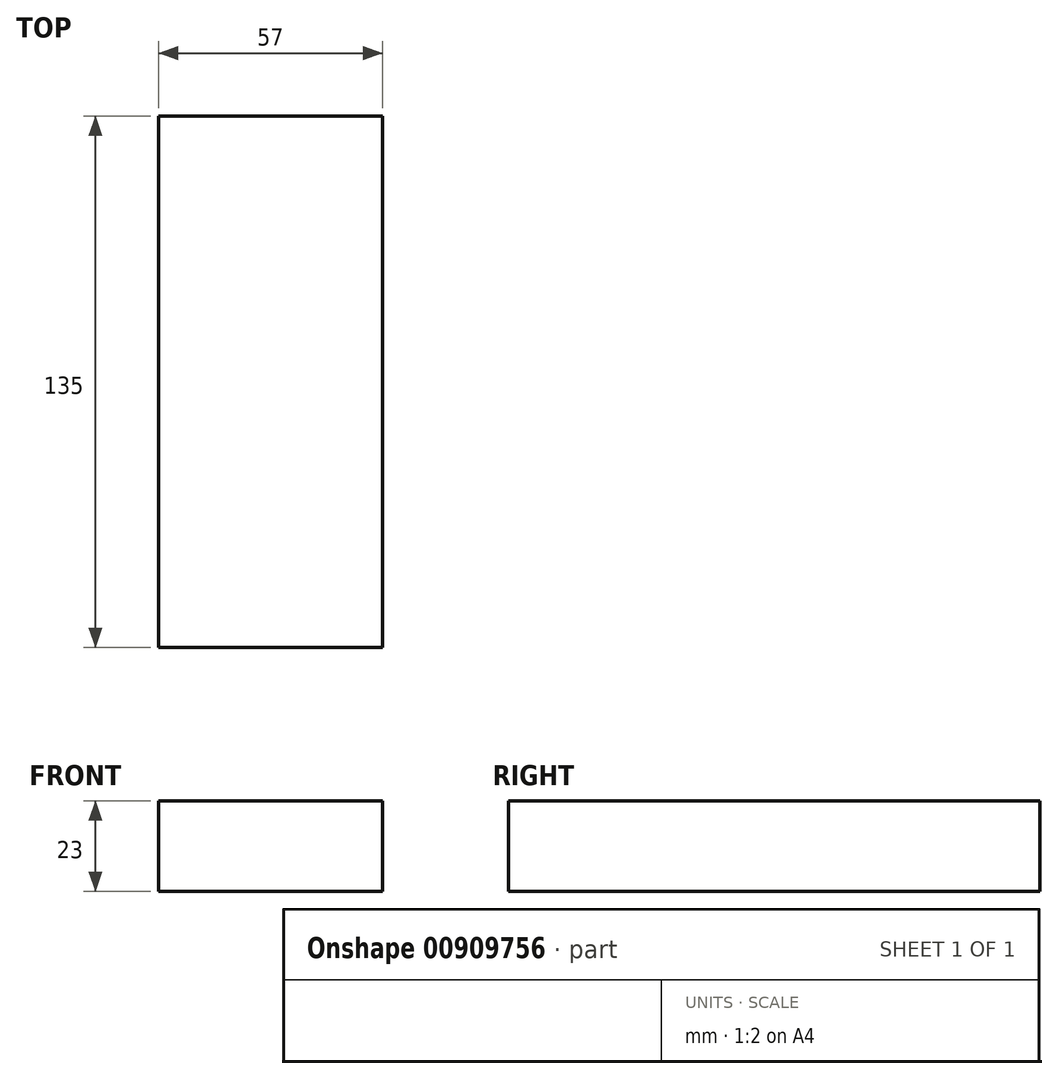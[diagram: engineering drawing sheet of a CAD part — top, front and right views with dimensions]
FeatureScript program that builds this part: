
annotation { "Feature Type Name" : "Feature", "Feature Type Description" : "" }
export const myFeature = defineFeature(function(context is Context, id is Id, definition is map)
    precondition{}
    {
        {
            var Q0;
            Q0=qCreatedBy(makeId("Top.planeOp"),FACE);
            var sketch = newSketch(context, id + "F0", { "sketchPlane" : qUnion([Q0])});
            skLineSegment(sketch, "E0.bottom", {"start": v(28.5, 67.5) * mm, "end": v(-28.5, 67.5) * mm});
            skLineSegment(sketch, "E0.top", {"start": v(28.5, -67.5) * mm, "end": v(-28.5, -67.5) * mm});
            skLineSegment(sketch, "E0.left", {"start": v(28.5, 67.5) * mm, "end": v(28.5, -67.5) * mm});
            skLineSegment(sketch, "E0.right", {"start": v(-28.5, 67.5) * mm, "end": v(-28.5, -67.5) * mm});
            skPoint(sketch, "E0.middle", {"position": v(0, 0) * mm});
            skSolve(sketch);
        }
        {
            var Q0;
            Q0 = qSketchRegion(id + "F0", true);
            extrude(context, id + "F1", {"entities" : qUnion([Q0]), "depth" : 23 * mm, "offsetDistance" : 25 * mm});
        }
    });
